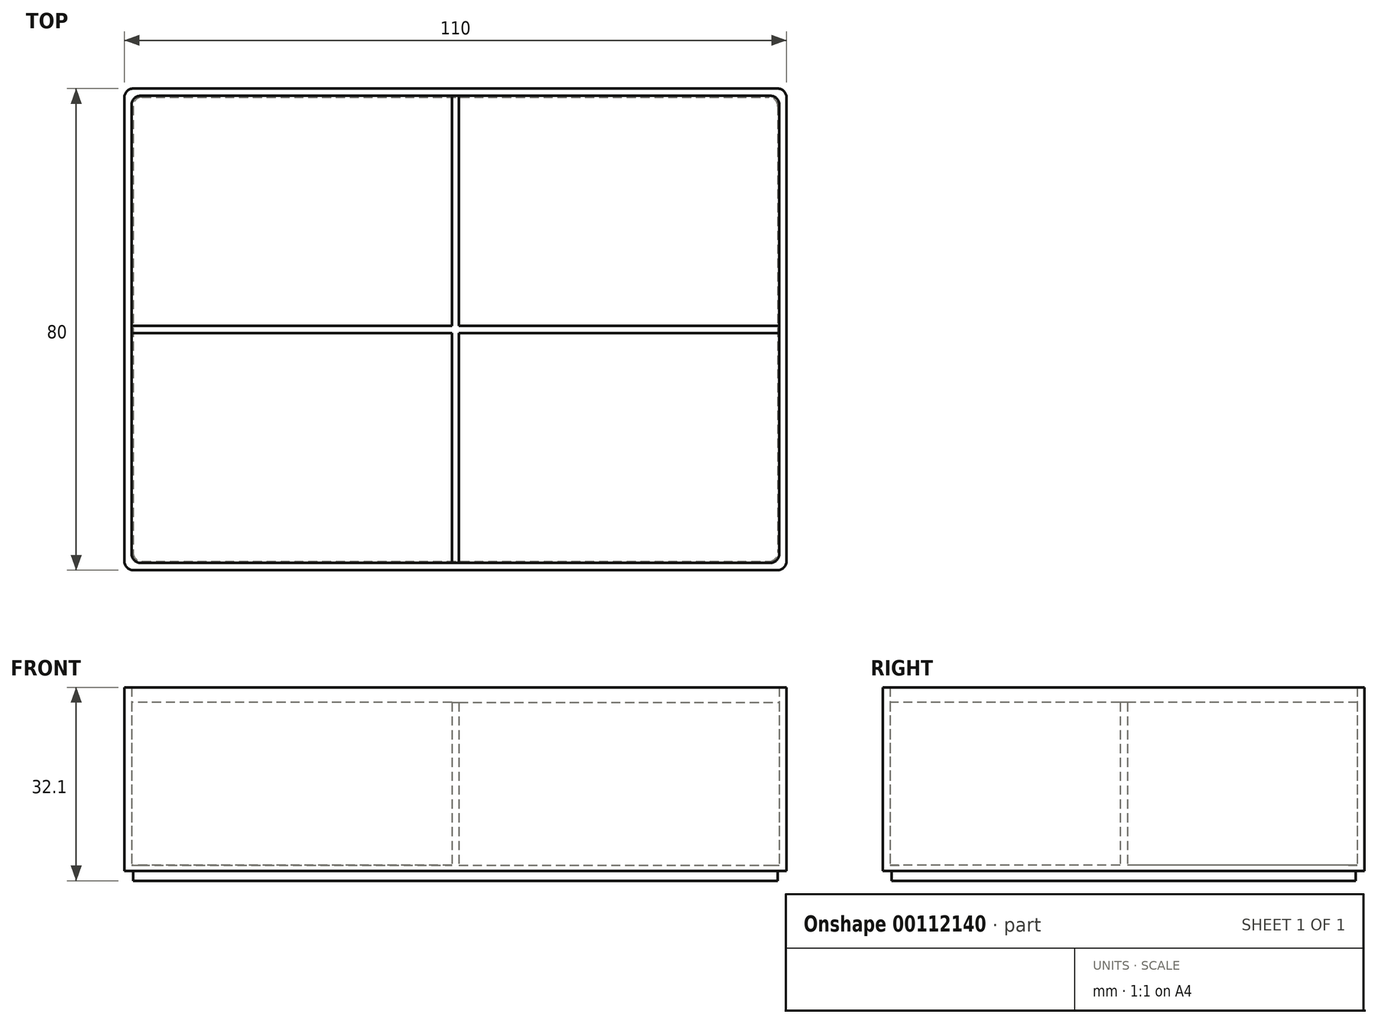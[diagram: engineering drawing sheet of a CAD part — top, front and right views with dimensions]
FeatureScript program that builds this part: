
annotation { "Feature Type Name" : "Feature", "Feature Type Description" : "" }
export const myFeature = defineFeature(function(context is Context, id is Id, definition is map)
    precondition{}
    {
        {
            var Q0;
            Q0=qCreatedBy(makeId("Top.planeOp"),FACE);
            var sketch = newSketch(context, id + "F0", { "sketchPlane" : qUnion([Q0])});
            skLineSegment(sketch, "E0.bottom", {"start": v(-73.3, 33.24) * mm, "end": v(36.7, 33.24) * mm});
            skLineSegment(sketch, "E0.top", {"start": v(-73.3, -46.76) * mm, "end": v(36.7, -46.76) * mm});
            skLineSegment(sketch, "E0.left", {"start": v(-73.3, 33.24) * mm, "end": v(-73.3, -46.76) * mm});
            skLineSegment(sketch, "E0.right", {"start": v(36.7, 33.24) * mm, "end": v(36.7, -46.76) * mm});
            skLineSegment(sketch, "E1.bottom", {"start": v(-72.1, 32.04) * mm, "end": v(35.5, 32.04) * mm});
            skLineSegment(sketch, "E1.top", {"start": v(-72.1, -45.56) * mm, "end": v(35.5, -45.56) * mm});
            skLineSegment(sketch, "E1.left", {"start": v(-72.1, 32.04) * mm, "end": v(-72.1, -45.56) * mm});
            skLineSegment(sketch, "E1.right", {"start": v(35.5, 32.04) * mm, "end": v(35.5, -45.56) * mm});
            skLineSegment(sketch, "E2.bottom", {"start": v(-71.84, 31.8) * mm, "end": v(35.26, 31.8) * mm});
            skLineSegment(sketch, "E2.top", {"start": v(-71.84, -45.3) * mm, "end": v(35.26, -45.3) * mm});
            skLineSegment(sketch, "E2.left", {"start": v(-71.84, 31.8) * mm, "end": v(-71.84, -45.3) * mm});
            skLineSegment(sketch, "E2.right", {"start": v(35.26, 31.8) * mm, "end": v(35.26, -45.3) * mm});
            skLineSegment(sketch, "E3", {"start": v(-72.1, -7.36) * mm, "end": v(35.5, -7.36) * mm});
            skLineSegment(sketch, "E4", {"start": v(35.5, -6.16) * mm, "end": v(-72.1, -6.16) * mm});
            skPoint(sketch, "E5", {"position": v(35.5, -6.76) * mm});
            skPoint(sketch, "E6", {"position": v(-18.3, -45.56) * mm});
            skLineSegment(sketch, "E7", {"start": v(-18.9, -45.56) * mm, "end": v(-18.9, 32.04) * mm});
            skLineSegment(sketch, "E8", {"start": v(-17.7, 32.04) * mm, "end": v(-17.7, -45.56) * mm});
            skSolve(sketch);
        }
        {
            var Q0;
            {var subQ5=sQuery(id+"F0.wireOp",EDGE,"E2.left");Q0=makeQuery(id+"F0.imprint","IMPRINT",FACE,{"disambiguationData":[TD([[makeQuery(id+"F0.imprint","IMPRINT",EDGE,{"derivedFrom":subQ5}),1.0]])]});}
            var Q1;
            {var subQ5=sQuery(id+"F0.wireOp",EDGE,"E2.right");Q1=makeQuery(id+"F0.imprint","IMPRINT",FACE,{"disambiguationData":[TD([[makeQuery(id+"F0.imprint","IMPRINT",EDGE,{"derivedFrom":subQ5}),-1.0]])]});}
            var Q2;
            {var subQ5=sQuery(id+"F0.wireOp",EDGE,"E1.left");Q2=makeQuery(id+"F0.imprint","IMPRINT",FACE,{"disambiguationData":[TD([[makeQuery(id+"F0.imprint","IMPRINT",EDGE,{"derivedFrom":subQ5}),1.0]])]});}
            var Q3;
            {var subQ0=sQuery(id+"F0.wireOp",EDGE,"DXXbI3K9-8nJS-BC3J-biNd-SqW7Ffo7gUfQ");var subQ1=sQuery(id+"F0.wireOp",EDGE,"E1.top");var subQ2=makeQuery(id+"F0.imprint","INTERSECT",VERTEX,{"derivedFrom":[subQ1,subQ0]});Q3=makeQuery(id+"F0.imprint","IMPRINT",FACE,{"disambiguationData":[TD([[makeQuery(id+"F0.imprint","IMPRINT",EDGE,{"disambiguationData":[TD([[subQ2,-1.0]])],"derivedFrom":subQ1}),1.0]])]});}
            var Q4;
            {var subQ6=sQuery(id+"F0.wireOp",EDGE,"E1.right");Q4=makeQuery(id+"F0.imprint","IMPRINT",FACE,{"disambiguationData":[TD([[makeQuery(id+"F0.imprint","IMPRINT",EDGE,{"derivedFrom":subQ6}),-1.0]])]});}
            var Q5;
            {var subQ0=sQuery(id+"F0.wireOp",EDGE,"DXXbI3K9-8nJS-BC3J-biNd-SqW7Ffo7gUfQ");var subQ1=sQuery(id+"F0.wireOp",EDGE,"E1.bottom");var subQ2=makeQuery(id+"F0.imprint","INTERSECT",VERTEX,{"derivedFrom":[subQ1,subQ0]});Q5=makeQuery(id+"F0.imprint","IMPRINT",FACE,{"disambiguationData":[TD([[makeQuery(id+"F0.imprint","IMPRINT",EDGE,{"disambiguationData":[TD([[subQ2,-1.0]])],"derivedFrom":subQ1}),-1.0]])]});}
            var Q6;
            {var subQ0=sQuery(id+"F0.wireOp",EDGE,"E2.bottom");var subQ1=sQuery(id+"F0.wireOp",EDGE,"DXXbI3K9-8nJS-BC3J-biNd-SqW7Ffo7gUfQ");var subQ2=makeQuery(id+"F0.imprint","INTERSECT",VERTEX,{"derivedFrom":[subQ1,subQ0]});Q6=makeQuery(id+"F0.imprint","IMPRINT",FACE,{"disambiguationData":[TD([[makeQuery(id+"F0.imprint","IMPRINT",EDGE,{"disambiguationData":[TD([[subQ2,-1.0]])],"derivedFrom":subQ1}),1.0]])]});}
            var Q7;
            {var subQ0=sQuery(id+"F0.wireOp",EDGE,"pcRSgDP9-UxY4-cM7n-EcvO-RXDttDQsLNeu");var subQ1=sQuery(id+"F0.wireOp",EDGE,"DXXbI3K9-8nJS-BC3J-biNd-SqW7Ffo7gUfQ");var subQ2=makeQuery(id+"F0.imprint","INTERSECT",VERTEX,{"derivedFrom":[subQ1,subQ0]});Q7=makeQuery(id+"F0.imprint","IMPRINT",FACE,{"disambiguationData":[TD([[makeQuery(id+"F0.imprint","IMPRINT",EDGE,{"disambiguationData":[TD([[subQ2,-1.0]])],"derivedFrom":subQ1}),1.0]])]});}
            var Q8;
            {var subQ0=sQuery(id+"F0.wireOp",EDGE,"4qyadx51-cw6L-Kn6I-lbK7-yWsqAp1ncPff");var subQ1=sQuery(id+"F0.wireOp",EDGE,"DXXbI3K9-8nJS-BC3J-biNd-SqW7Ffo7gUfQ");var subQ2=makeQuery(id+"F0.imprint","INTERSECT",VERTEX,{"derivedFrom":[subQ1,subQ0]});Q8=makeQuery(id+"F0.imprint","IMPRINT",FACE,{"disambiguationData":[TD([[makeQuery(id+"F0.imprint","IMPRINT",EDGE,{"disambiguationData":[TD([[subQ2,-1.0]])],"derivedFrom":subQ1}),1.0]])]});}
            var Q9;
            {var subQ5=sQuery(id+"F0.wireOp",EDGE,"E1.bottom");var subQ7=sQuery(id+"F0.wireOp",EDGE,"E1.left");var subQ8=makeQuery(id+"F0.imprint","INTERSECT",VERTEX,{"derivedFrom":[subQ5,subQ7]});Q9=makeQuery(id+"F0.imprint","IMPRINT",FACE,{"disambiguationData":[TD([[makeQuery(id+"F0.imprint","IMPRINT",EDGE,{"disambiguationData":[TD([[subQ8,-1.0]])],"derivedFrom":subQ5}),-1.0]])]});}
            var Q10;
            {var subQ7=sQuery(id+"F0.wireOp",EDGE,"E1.top");var subQ9=sQuery(id+"F0.wireOp",EDGE,"E1.right");var subQ10=makeQuery(id+"F0.imprint","INTERSECT",VERTEX,{"derivedFrom":[subQ7,subQ9]});Q10=makeQuery(id+"F0.imprint","IMPRINT",FACE,{"disambiguationData":[TD([[makeQuery(id+"F0.imprint","IMPRINT",EDGE,{"disambiguationData":[TD([[subQ10,1.0]])],"derivedFrom":subQ7}),1.0]])]});}
            var Q11;
            {var subQ0=sQuery(id+"F0.wireOp",EDGE,"E7");var subQ1=sQuery(id+"F0.wireOp",EDGE,"E2.bottom");var subQ2=makeQuery(id+"F0.imprint","INTERSECT",VERTEX,{"derivedFrom":[subQ1,subQ0]});Q11=makeQuery(id+"F0.imprint","IMPRINT",FACE,{"disambiguationData":[TD([[makeQuery(id+"F0.imprint","IMPRINT",EDGE,{"disambiguationData":[TD([[subQ2,-1.0]])],"derivedFrom":subQ1}),-1.0]])]});}
            var Q12;
            {var subQ0=sQuery(id+"F0.wireOp",EDGE,"E7");var subQ1=sQuery(id+"F0.wireOp",EDGE,"E3");var subQ2=makeQuery(id+"F0.imprint","INTERSECT",VERTEX,{"derivedFrom":[subQ1,subQ0]});Q12=makeQuery(id+"F0.imprint","IMPRINT",FACE,{"disambiguationData":[TD([[makeQuery(id+"F0.imprint","IMPRINT",EDGE,{"disambiguationData":[TD([[subQ2,-1.0]])],"derivedFrom":subQ1}),1.0]])]});}
            var Q13;
            {var subQ0=sQuery(id+"F0.wireOp",EDGE,"E7");var subQ1=sQuery(id+"F0.wireOp",EDGE,"E2.top");var subQ2=makeQuery(id+"F0.imprint","INTERSECT",VERTEX,{"derivedFrom":[subQ1,subQ0]});Q13=makeQuery(id+"F0.imprint","IMPRINT",FACE,{"disambiguationData":[TD([[makeQuery(id+"F0.imprint","IMPRINT",EDGE,{"disambiguationData":[TD([[subQ2,-1.0]])],"derivedFrom":subQ1}),1.0]])]});}
            var Q14;
            {var subQ7=sQuery(id+"F0.wireOp",EDGE,"E1.right");var subQ8=sQuery(id+"F0.wireOp",EDGE,"E1.bottom");var subQ9=makeQuery(id+"F0.imprint","INTERSECT",VERTEX,{"derivedFrom":[subQ8,subQ7]});Q14=makeQuery(id+"F0.imprint","IMPRINT",FACE,{"disambiguationData":[TD([[makeQuery(id+"F0.imprint","IMPRINT",EDGE,{"disambiguationData":[TD([[subQ9,1.0]])],"derivedFrom":subQ8}),-1.0]])]});}
            var Q15;
            {var subQ6=sQuery(id+"F0.wireOp",EDGE,"E1.top");var subQ9=sQuery(id+"F0.wireOp",EDGE,"E1.left");var subQ10=makeQuery(id+"F0.imprint","INTERSECT",VERTEX,{"derivedFrom":[subQ6,subQ9]});Q15=makeQuery(id+"F0.imprint","IMPRINT",FACE,{"disambiguationData":[TD([[makeQuery(id+"F0.imprint","IMPRINT",EDGE,{"disambiguationData":[TD([[subQ10,-1.0]])],"derivedFrom":subQ6}),1.0]])]});}
            extrude(context, id + "F1", {"entities" : qUnion([Q0, Q1, Q2, Q3, Q4, Q5, Q6, Q7, Q8, Q9, Q10, Q11, Q12, Q13, Q14, Q15]), "depth" : 1 * mm});
        }
        {
            var Q0;
            {var subQ0=sQuery(id+"F0.wireOp",EDGE,"E2.bottom");var subQ1=sQuery(id+"F0.wireOp",EDGE,"DXXbI3K9-8nJS-BC3J-biNd-SqW7Ffo7gUfQ");var subQ2=makeQuery(id+"F0.imprint","INTERSECT",VERTEX,{"derivedFrom":[subQ1,subQ0]});Q0=makeQuery(id+"F0.imprint","IMPRINT",FACE,{"disambiguationData":[TD([[makeQuery(id+"F0.imprint","IMPRINT",EDGE,{"disambiguationData":[TD([[subQ2,-1.0]])],"derivedFrom":subQ1}),1.0]])]});}
            var Q1;
            {var subQ0=sQuery(id+"F0.wireOp",EDGE,"DXXbI3K9-8nJS-BC3J-biNd-SqW7Ffo7gUfQ");var subQ1=sQuery(id+"F0.wireOp",EDGE,"E1.top");var subQ2=makeQuery(id+"F0.imprint","INTERSECT",VERTEX,{"derivedFrom":[subQ1,subQ0]});Q1=makeQuery(id+"F0.imprint","IMPRINT",FACE,{"disambiguationData":[TD([[makeQuery(id+"F0.imprint","IMPRINT",EDGE,{"disambiguationData":[TD([[subQ2,-1.0]])],"derivedFrom":subQ1}),1.0]])]});}
            var Q2;
            {var subQ0=sQuery(id+"F0.wireOp",EDGE,"pcRSgDP9-UxY4-cM7n-EcvO-RXDttDQsLNeu");var subQ1=sQuery(id+"F0.wireOp",EDGE,"DXXbI3K9-8nJS-BC3J-biNd-SqW7Ffo7gUfQ");var subQ2=makeQuery(id+"F0.imprint","INTERSECT",VERTEX,{"derivedFrom":[subQ1,subQ0]});Q2=makeQuery(id+"F0.imprint","IMPRINT",FACE,{"disambiguationData":[TD([[makeQuery(id+"F0.imprint","IMPRINT",EDGE,{"disambiguationData":[TD([[subQ2,-1.0]])],"derivedFrom":subQ1}),-1.0]])]});}
            var Q3;
            {var subQ0=sQuery(id+"F0.wireOp",EDGE,"pcRSgDP9-UxY4-cM7n-EcvO-RXDttDQsLNeu");var subQ1=sQuery(id+"F0.wireOp",EDGE,"DXXbI3K9-8nJS-BC3J-biNd-SqW7Ffo7gUfQ");var subQ2=makeQuery(id+"F0.imprint","INTERSECT",VERTEX,{"derivedFrom":[subQ1,subQ0]});Q3=makeQuery(id+"F0.imprint","IMPRINT",FACE,{"disambiguationData":[TD([[makeQuery(id+"F0.imprint","IMPRINT",EDGE,{"disambiguationData":[TD([[subQ2,-1.0]])],"derivedFrom":subQ1}),1.0]])]});}
            var Q4;
            {var subQ0=sQuery(id+"F0.wireOp",EDGE,"pcRSgDP9-UxY4-cM7n-EcvO-RXDttDQsLNeu");var subQ1=sQuery(id+"F0.wireOp",EDGE,"CcxUEpOw-EvIM-Vnl9-Mv94-KDQ5p1Qi4Pa2");var subQ2=makeQuery(id+"F0.imprint","INTERSECT",VERTEX,{"derivedFrom":[subQ1,subQ0]});Q4=makeQuery(id+"F0.imprint","IMPRINT",FACE,{"disambiguationData":[TD([[makeQuery(id+"F0.imprint","IMPRINT",EDGE,{"disambiguationData":[TD([[subQ2,-1.0]])],"derivedFrom":subQ1}),1.0]])]});}
            var Q5;
            {var subQ0=sQuery(id+"F0.wireOp",EDGE,"4qyadx51-cw6L-Kn6I-lbK7-yWsqAp1ncPff");var subQ1=sQuery(id+"F0.wireOp",EDGE,"DXXbI3K9-8nJS-BC3J-biNd-SqW7Ffo7gUfQ");var subQ2=makeQuery(id+"F0.imprint","INTERSECT",VERTEX,{"derivedFrom":[subQ1,subQ0]});Q5=makeQuery(id+"F0.imprint","IMPRINT",FACE,{"disambiguationData":[TD([[makeQuery(id+"F0.imprint","IMPRINT",EDGE,{"disambiguationData":[TD([[subQ2,-1.0]])],"derivedFrom":subQ1}),1.0]])]});}
            var Q6;
            {var subQ0=sQuery(id+"F0.wireOp",EDGE,"E7");var subQ1=sQuery(id+"F0.wireOp",EDGE,"E2.top");var subQ2=makeQuery(id+"F0.imprint","INTERSECT",VERTEX,{"derivedFrom":[subQ1,subQ0]});Q6=makeQuery(id+"F0.imprint","IMPRINT",FACE,{"disambiguationData":[TD([[makeQuery(id+"F0.imprint","IMPRINT",EDGE,{"disambiguationData":[TD([[subQ2,-1.0]])],"derivedFrom":subQ1}),1.0]])]});}
            var Q7;
            {var subQ0=sQuery(id+"F0.wireOp",EDGE,"E4");var subQ1=sQuery(id+"F0.wireOp",EDGE,"E2.left");var subQ2=makeQuery(id+"F0.imprint","INTERSECT",VERTEX,{"derivedFrom":[subQ1,subQ0]});Q7=makeQuery(id+"F0.imprint","IMPRINT",FACE,{"disambiguationData":[TD([[makeQuery(id+"F0.imprint","IMPRINT",EDGE,{"disambiguationData":[TD([[subQ2,-1.0]])],"derivedFrom":subQ1}),1.0]])]});}
            var Q8;
            {var subQ0=sQuery(id+"F0.wireOp",EDGE,"E7");var subQ1=sQuery(id+"F0.wireOp",EDGE,"E3");var subQ2=makeQuery(id+"F0.imprint","INTERSECT",VERTEX,{"derivedFrom":[subQ1,subQ0]});Q8=makeQuery(id+"F0.imprint","IMPRINT",FACE,{"disambiguationData":[TD([[makeQuery(id+"F0.imprint","IMPRINT",EDGE,{"disambiguationData":[TD([[subQ2,-1.0]])],"derivedFrom":subQ1}),1.0]])]});}
            var Q9;
            {var subQ0=sQuery(id+"F0.wireOp",EDGE,"E4");var subQ1=sQuery(id+"F0.wireOp",EDGE,"E2.right");var subQ2=makeQuery(id+"F0.imprint","INTERSECT",VERTEX,{"derivedFrom":[subQ1,subQ0]});Q9=makeQuery(id+"F0.imprint","IMPRINT",FACE,{"disambiguationData":[TD([[makeQuery(id+"F0.imprint","IMPRINT",EDGE,{"disambiguationData":[TD([[subQ2,-1.0]])],"derivedFrom":subQ1}),-1.0]])]});}
            var Q10;
            {var subQ0=sQuery(id+"F0.wireOp",EDGE,"E7");var subQ1=sQuery(id+"F0.wireOp",EDGE,"E2.bottom");var subQ2=makeQuery(id+"F0.imprint","INTERSECT",VERTEX,{"derivedFrom":[subQ1,subQ0]});Q10=makeQuery(id+"F0.imprint","IMPRINT",FACE,{"disambiguationData":[TD([[makeQuery(id+"F0.imprint","IMPRINT",EDGE,{"disambiguationData":[TD([[subQ2,-1.0]])],"derivedFrom":subQ1}),-1.0]])]});}
            var Q11;
            {var subQ0=sQuery(id+"F0.wireOp",EDGE,"E3");var subQ1=sQuery(id+"F0.wireOp",EDGE,"E1.left");var subQ2=makeQuery(id+"F0.imprint","INTERSECT",VERTEX,{"derivedFrom":[subQ1,subQ0]});Q11=makeQuery(id+"F0.imprint","IMPRINT",FACE,{"disambiguationData":[TD([[makeQuery(id+"F0.imprint","IMPRINT",EDGE,{"disambiguationData":[TD([[subQ2,1.0]])],"derivedFrom":subQ1}),1.0]])]});}
            var Q12;
            {var subQ0=sQuery(id+"F0.wireOp",EDGE,"E3");var subQ1=sQuery(id+"F0.wireOp",EDGE,"E1.right");var subQ2=makeQuery(id+"F0.imprint","INTERSECT",VERTEX,{"derivedFrom":[subQ1,subQ0]});Q12=makeQuery(id+"F0.imprint","IMPRINT",FACE,{"disambiguationData":[TD([[makeQuery(id+"F0.imprint","IMPRINT",EDGE,{"disambiguationData":[TD([[subQ2,1.0]])],"derivedFrom":subQ1}),-1.0]])]});}
            var Q13;
            {var subQ0=sQuery(id+"F0.wireOp",EDGE,"E7");var subQ1=sQuery(id+"F0.wireOp",EDGE,"E1.bottom");var subQ2=makeQuery(id+"F0.imprint","INTERSECT",VERTEX,{"derivedFrom":[subQ1,subQ0]});Q13=makeQuery(id+"F0.imprint","IMPRINT",FACE,{"disambiguationData":[TD([[makeQuery(id+"F0.imprint","IMPRINT",EDGE,{"disambiguationData":[TD([[subQ2,-1.0]])],"derivedFrom":subQ1}),-1.0]])]});}
            extrude(context, id + "F2", {"entities" : qUnion([Q0, Q1, Q2, Q3, Q4, Q5, Q6, Q7, Q8, Q9, Q10, Q11, Q12, Q13]), "operationType" : NewBodyOperationType.ADD, "depth" : 28 * mm});
        }
        {
            var Q0;
            {var subQ4=sQuery(id+"F0.wireOp",EDGE,"E0.left");Q0=makeQuery(id+"F0.imprint","IMPRINT",FACE,{"disambiguationData":[TD([[makeQuery(id+"F0.imprint","IMPRINT",EDGE,{"derivedFrom":subQ4}),1.0]])]});}
            var Q1;
            {var subQ0=sQuery(id+"F0.wireOp",EDGE,"DXXbI3K9-8nJS-BC3J-biNd-SqW7Ffo7gUfQ");var subQ1=sQuery(id+"F0.wireOp",EDGE,"E0.bottom");var subQ2=makeQuery(id+"F0.imprint","INTERSECT",VERTEX,{"derivedFrom":[subQ1,subQ0]});Q1=makeQuery(id+"F0.imprint","IMPRINT",FACE,{"disambiguationData":[TD([[makeQuery(id+"F0.imprint","IMPRINT",EDGE,{"disambiguationData":[TD([[subQ2,-1.0]])],"derivedFrom":subQ1}),-1.0]])]});}
            var Q2;
            {var subQ4=sQuery(id+"F0.wireOp",EDGE,"E0.right");Q2=makeQuery(id+"F0.imprint","IMPRINT",FACE,{"disambiguationData":[TD([[makeQuery(id+"F0.imprint","IMPRINT",EDGE,{"derivedFrom":subQ4}),-1.0]])]});}
            var Q3;
            {var subQ0=sQuery(id+"F0.wireOp",EDGE,"DXXbI3K9-8nJS-BC3J-biNd-SqW7Ffo7gUfQ");var subQ1=sQuery(id+"F0.wireOp",EDGE,"E0.top");var subQ2=makeQuery(id+"F0.imprint","INTERSECT",VERTEX,{"derivedFrom":[subQ1,subQ0]});Q3=makeQuery(id+"F0.imprint","IMPRINT",FACE,{"disambiguationData":[TD([[makeQuery(id+"F0.imprint","IMPRINT",EDGE,{"disambiguationData":[TD([[subQ2,-1.0]])],"derivedFrom":subQ1}),1.0]])]});}
            extrude(context, id + "F3", {"entities" : qUnion([Q0, Q1, Q2, Q3]), "operationType" : NewBodyOperationType.ADD, "depth" : 30.5 * mm});
        }
        {
            var Q0;
            {var subQ5=sQuery(id+"F0.wireOp",EDGE,"E2.left");Q0=makeQuery(id+"F0.imprint","IMPRINT",FACE,{"disambiguationData":[TD([[makeQuery(id+"F0.imprint","IMPRINT",EDGE,{"derivedFrom":subQ5}),1.0]])]});}
            var Q1;
            {var subQ0=sQuery(id+"F0.wireOp",EDGE,"E2.bottom");var subQ1=sQuery(id+"F0.wireOp",EDGE,"DXXbI3K9-8nJS-BC3J-biNd-SqW7Ffo7gUfQ");var subQ2=makeQuery(id+"F0.imprint","INTERSECT",VERTEX,{"derivedFrom":[subQ1,subQ0]});Q1=makeQuery(id+"F0.imprint","IMPRINT",FACE,{"disambiguationData":[TD([[makeQuery(id+"F0.imprint","IMPRINT",EDGE,{"disambiguationData":[TD([[subQ2,-1.0]])],"derivedFrom":subQ1}),1.0]])]});}
            var Q2;
            {var subQ5=sQuery(id+"F0.wireOp",EDGE,"E2.right");Q2=makeQuery(id+"F0.imprint","IMPRINT",FACE,{"disambiguationData":[TD([[makeQuery(id+"F0.imprint","IMPRINT",EDGE,{"derivedFrom":subQ5}),-1.0]])]});}
            var Q3;
            {var subQ0=sQuery(id+"F0.wireOp",EDGE,"E7");var subQ1=sQuery(id+"F0.wireOp",EDGE,"E2.top");var subQ2=makeQuery(id+"F0.imprint","INTERSECT",VERTEX,{"derivedFrom":[subQ1,subQ0]});Q3=makeQuery(id+"F0.imprint","IMPRINT",FACE,{"disambiguationData":[TD([[makeQuery(id+"F0.imprint","IMPRINT",EDGE,{"disambiguationData":[TD([[subQ2,-1.0]])],"derivedFrom":subQ1}),1.0]])]});}
            var Q4;
            {var subQ0=sQuery(id+"F0.wireOp",EDGE,"E7");var subQ1=sQuery(id+"F0.wireOp",EDGE,"E2.bottom");var subQ2=makeQuery(id+"F0.imprint","INTERSECT",VERTEX,{"derivedFrom":[subQ1,subQ0]});Q4=makeQuery(id+"F0.imprint","IMPRINT",FACE,{"disambiguationData":[TD([[makeQuery(id+"F0.imprint","IMPRINT",EDGE,{"disambiguationData":[TD([[subQ2,-1.0]])],"derivedFrom":subQ1}),-1.0]])]});}
            var Q5;
            {var subQ0=sQuery(id+"F0.wireOp",EDGE,"E7");var subQ1=sQuery(id+"F0.wireOp",EDGE,"E3");var subQ2=makeQuery(id+"F0.imprint","INTERSECT",VERTEX,{"derivedFrom":[subQ1,subQ0]});Q5=makeQuery(id+"F0.imprint","IMPRINT",FACE,{"disambiguationData":[TD([[makeQuery(id+"F0.imprint","IMPRINT",EDGE,{"disambiguationData":[TD([[subQ2,-1.0]])],"derivedFrom":subQ1}),1.0]])]});}
            extrude(context, id + "F4", {"entities" : qUnion([Q0, Q1, Q2, Q3, Q4, Q5]), "operationType" : NewBodyOperationType.ADD, "oppositeDirection" : true, "depth" : 1.6 * mm});
        }
        {
            var Q0;
            Q0=makeQuery(id+"F3.opExtrude","SWEPT_EDGE",EDGE,{"disambiguationData":[OSD([sQuery(id+"F0.wireOp",EDGE,"E1.bottom"),sQuery(id+"F0.wireOp",EDGE,"E1.left")])]});
            var Q1;
            {var subQ0=sQuery(id+"F0.wireOp",EDGE,"E1.left");var subQ1=sQuery(id+"F0.wireOp",EDGE,"E1.bottom");Q1=makeQuery(id+"F3.boolean.opBoolean","SPLIT",EDGE,{"disambiguationData":[TD([makeQuery(id+"F3.opExtrude","SWEPT_FACE",FACE,{"disambiguationData":[OSD([subQ0])]})])],"derivedFrom":makeQuery(id+"F1.opExtrude","CAP_EDGE",EDGE,{"disambiguationData":[OSD([subQ1])],"isStart":false})});}
            var Q2;
            Q2=makeQuery(id+"F1.opExtrude","CAP_EDGE",EDGE,{"disambiguationData":[OSD([sQuery(id+"F0.wireOp",EDGE,"E1.left")])],"isStart":false});
            var Q3;
            {var subQ0=sQuery(id+"F0.wireOp",EDGE,"E1.right");var subQ1=sQuery(id+"F0.wireOp",EDGE,"E1.bottom");Q3=makeQuery(id+"F3.boolean.opBoolean","SPLIT",EDGE,{"disambiguationData":[TD([makeQuery(id+"F3.opExtrude","SWEPT_FACE",FACE,{"disambiguationData":[OSD([subQ0])]})])],"derivedFrom":makeQuery(id+"F1.opExtrude","CAP_EDGE",EDGE,{"disambiguationData":[OSD([subQ1])],"isStart":false})});}
            var Q4;
            Q4=makeQuery(id+"F3.opExtrude","SWEPT_EDGE",EDGE,{"disambiguationData":[OSD([sQuery(id+"F0.wireOp",EDGE,"E1.bottom"),sQuery(id+"F0.wireOp",EDGE,"E1.right")])]});
            var Q5;
            Q5=makeQuery(id+"F1.opExtrude","CAP_EDGE",EDGE,{"disambiguationData":[OSD([sQuery(id+"F0.wireOp",EDGE,"E1.right")])],"isStart":false});
            var Q6;
            {var subQ0=sQuery(id+"F0.wireOp",EDGE,"E1.right");var subQ1=sQuery(id+"F0.wireOp",EDGE,"E1.top");Q6=makeQuery(id+"F3.boolean.opBoolean","SPLIT",EDGE,{"disambiguationData":[TD([makeQuery(id+"F3.opExtrude","SWEPT_FACE",FACE,{"disambiguationData":[OSD([subQ0])]})])],"derivedFrom":makeQuery(id+"F1.opExtrude","CAP_EDGE",EDGE,{"disambiguationData":[OSD([subQ1])],"isStart":false})});}
            var Q7;
            Q7=makeQuery(id+"F3.opExtrude","SWEPT_EDGE",EDGE,{"disambiguationData":[OSD([sQuery(id+"F0.wireOp",EDGE,"E1.top"),sQuery(id+"F0.wireOp",EDGE,"E1.right")])]});
            var Q8;
            {var subQ0=sQuery(id+"F0.wireOp",EDGE,"E1.left");var subQ1=sQuery(id+"F0.wireOp",EDGE,"E1.top");Q8=makeQuery(id+"F3.boolean.opBoolean","SPLIT",EDGE,{"disambiguationData":[TD([makeQuery(id+"F3.opExtrude","SWEPT_FACE",FACE,{"disambiguationData":[OSD([subQ0])]})])],"derivedFrom":makeQuery(id+"F1.opExtrude","CAP_EDGE",EDGE,{"disambiguationData":[OSD([subQ1])],"isStart":false})});}
            var Q9;
            Q9=makeQuery(id+"F3.opExtrude","SWEPT_EDGE",EDGE,{"disambiguationData":[OSD([sQuery(id+"F0.wireOp",EDGE,"E1.top"),sQuery(id+"F0.wireOp",EDGE,"E1.left")])]});
            var Q10;
            Q10=makeQuery(id+"F3.opExtrude","SWEPT_EDGE",EDGE,{"disambiguationData":[OSD([sQuery(id+"F0.wireOp",EDGE,"E0.top"),sQuery(id+"F0.wireOp",EDGE,"E0.right")])]});
            var Q11;
            Q11=makeQuery(id+"F3.opExtrude","SWEPT_EDGE",EDGE,{"disambiguationData":[OSD([sQuery(id+"F0.wireOp",EDGE,"E0.top"),sQuery(id+"F0.wireOp",EDGE,"E0.left")])]});
            var Q12;
            Q12=makeQuery(id+"F3.opExtrude","SWEPT_EDGE",EDGE,{"disambiguationData":[OSD([sQuery(id+"F0.wireOp",EDGE,"E0.bottom"),sQuery(id+"F0.wireOp",EDGE,"E0.left")])]});
            var Q13;
            Q13=makeQuery(id+"F3.opExtrude","SWEPT_EDGE",EDGE,{"disambiguationData":[OSD([sQuery(id+"F0.wireOp",EDGE,"E0.bottom"),sQuery(id+"F0.wireOp",EDGE,"E0.right")])]});
            var Q14;
            Q14=makeQuery(id+"F4.opExtrude","SWEPT_EDGE",EDGE,{"disambiguationData":[OSD([sQuery(id+"F0.wireOp",EDGE,"E2.top"),sQuery(id+"F0.wireOp",EDGE,"E2.left")])]});
            var Q15;
            Q15=makeQuery(id+"F4.opExtrude","SWEPT_EDGE",EDGE,{"disambiguationData":[OSD([sQuery(id+"F0.wireOp",EDGE,"E2.top"),sQuery(id+"F0.wireOp",EDGE,"E2.right")])]});
            var Q16;
            Q16=makeQuery(id+"F4.opExtrude","SWEPT_EDGE",EDGE,{"disambiguationData":[OSD([sQuery(id+"F0.wireOp",EDGE,"E2.bottom"),sQuery(id+"F0.wireOp",EDGE,"E2.right")])]});
            var Q17;
            Q17=makeQuery(id+"F4.opExtrude","SWEPT_EDGE",EDGE,{"disambiguationData":[OSD([sQuery(id+"F0.wireOp",EDGE,"E2.bottom"),sQuery(id+"F0.wireOp",EDGE,"E2.left")])]});
            fillet(context, id + "F5", {"entities" : qUnion([Q0, Q1, Q2, Q3, Q4, Q5, Q6, Q7, Q8, Q9, Q10, Q11, Q12, Q13, Q14, Q15, Q16, Q17]), "radius" : 1.5 * mm, "tangentPropagation" : true, "allowEdgeOverflow" : false});
        }
    });
